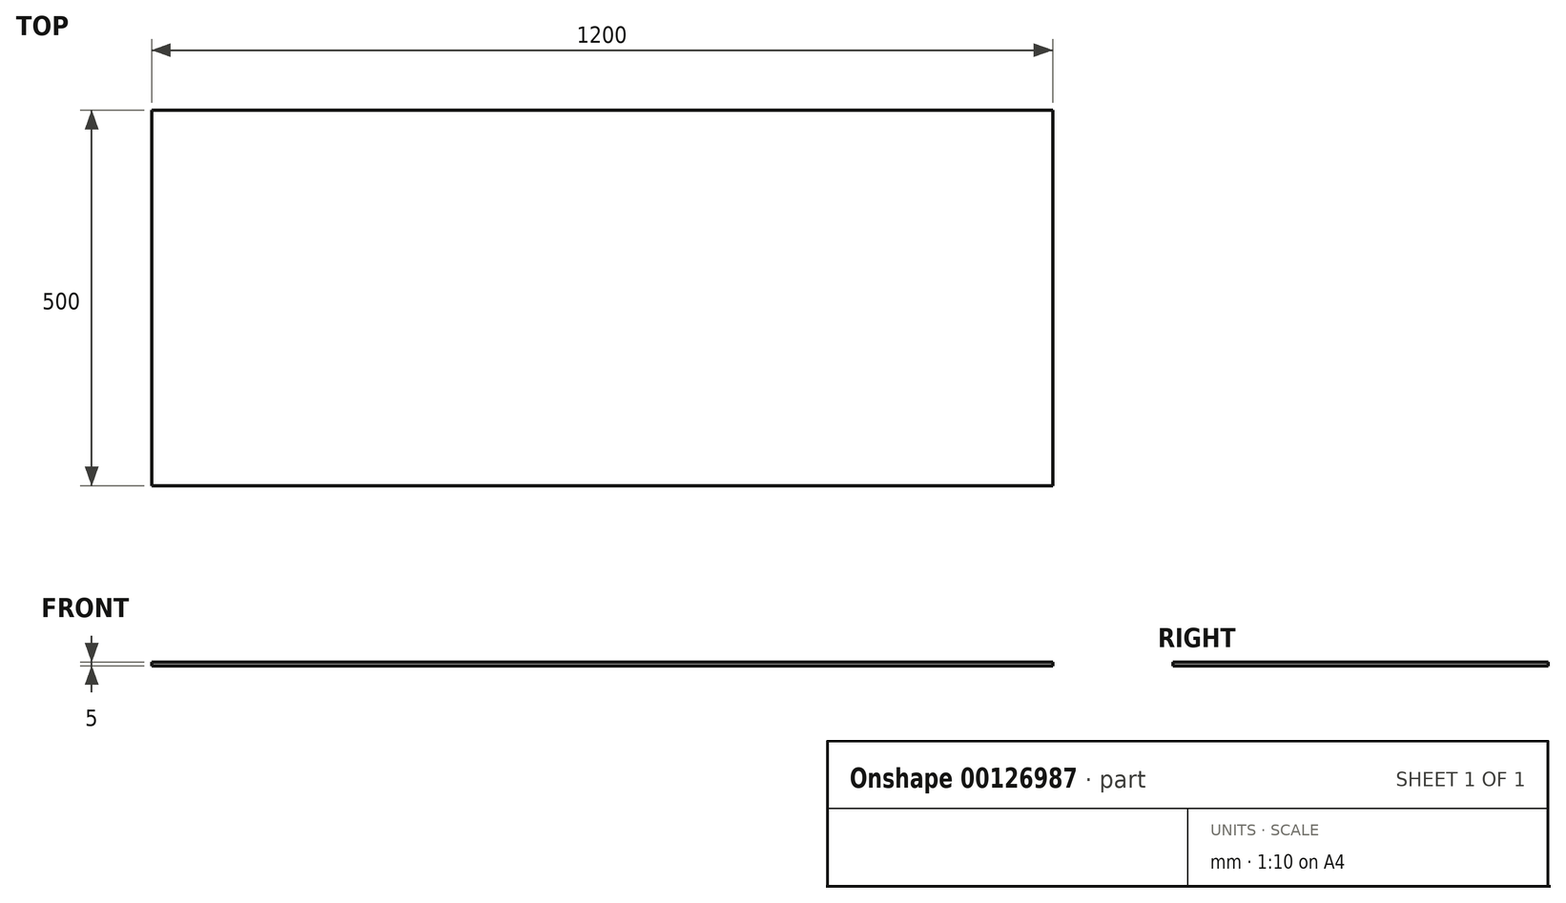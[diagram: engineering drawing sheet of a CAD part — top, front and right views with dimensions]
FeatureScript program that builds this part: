
annotation { "Feature Type Name" : "Feature", "Feature Type Description" : "" }
export const myFeature = defineFeature(function(context is Context, id is Id, definition is map)
    precondition{}
    {
        {
            var Q0;
            Q0=qCreatedBy(makeId("Top.planeOp"),FACE);
            var sketch = newSketch(context, id + "F0", { "sketchPlane" : qUnion([Q0])});
            skLineSegment(sketch, "E0.bottom", {"start": v(0, 0) * mm, "end": v(1200, 0) * mm});
            skLineSegment(sketch, "E0.top", {"start": v(0, 500) * mm, "end": v(1200, 500) * mm});
            skLineSegment(sketch, "E0.left", {"start": v(0, 0) * mm, "end": v(0, 500) * mm});
            skLineSegment(sketch, "E0.right", {"start": v(1200, 0) * mm, "end": v(1200, 500) * mm});
            skSolve(sketch);
        }
        {
            var Q0;
            Q0 = qSketchRegion(id + "F0", true);
            extrude(context, id + "F1", {"entities" : qUnion([Q0]), "depth" : 5 * mm});
        }
    });
